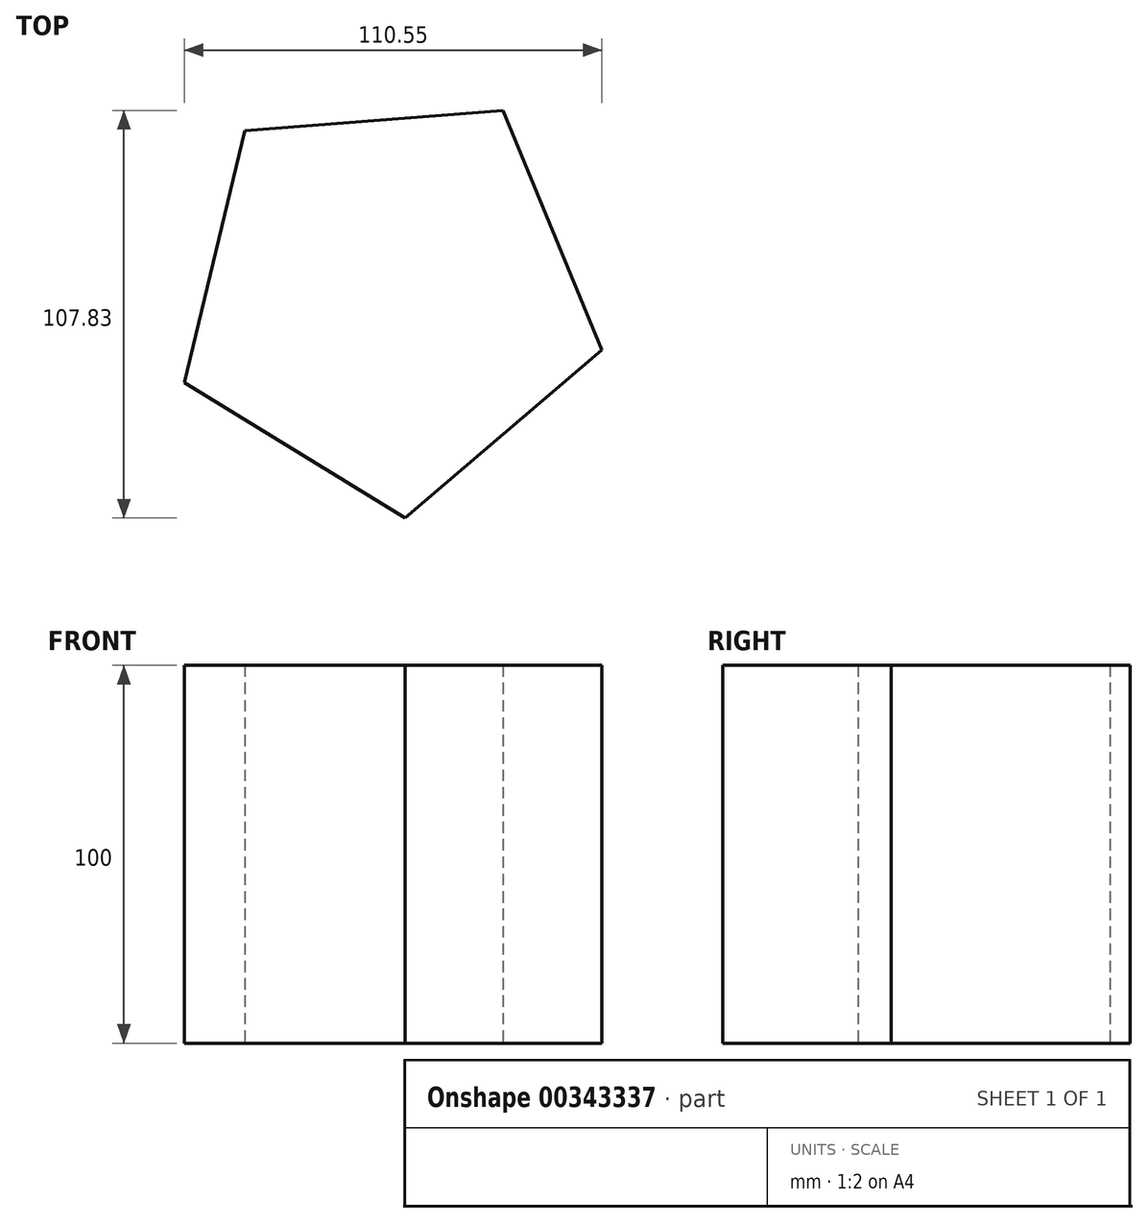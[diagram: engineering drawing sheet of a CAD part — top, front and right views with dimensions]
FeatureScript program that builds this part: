
annotation { "Feature Type Name" : "Feature", "Feature Type Description" : "" }
export const myFeature = defineFeature(function(context is Context, id is Id, definition is map)
    precondition{}
    {
        {
            var Q0;
            Q0=qCreatedBy(makeId("Top.planeOp"),FACE);
            var sketch = newSketch(context, id + "F0", { "sketchPlane" : qUnion([Q0])});
            skCircle(sketch, "E0.cCircle", {"center": v(0, 0) * mm, "radius": 58.3 * mm, "construction": true});
            skLineSegment(sketch, "E0.0", {"start": v(-37.87, 44.32) * mm, "end": v(30.45, 49.71) * mm});
            skLineSegment(sketch, "E0.1", {"start": v(30.45, 49.71) * mm, "end": v(56.69, -13.6) * mm});
            skLineSegment(sketch, "E0.2", {"start": v(56.69, -13.6) * mm, "end": v(4.58, -58.12) * mm});
            skLineSegment(sketch, "E0.3", {"start": v(4.58, -58.12) * mm, "end": v(-53.86, -22.32) * mm});
            skLineSegment(sketch, "E0.4", {"start": v(-53.86, -22.32) * mm, "end": v(-37.87, 44.32) * mm});
            skSolve(sketch);
        }
        {
            var Q0;
            Q0=makeQuery(id+"F0.imprint","IMPRINT",FACE,{"disambiguationData":[TD([[makeQuery(id+"F0.imprint","IMPRINT",EDGE,{"derivedFrom":sQuery(id+"F0.wireOp",EDGE,"E0.0")}),-1.0]])]});
            extrude(context, id + "F1", {"entities" : qUnion([Q0]), "depth" : 100 * mm});
        }
    });
